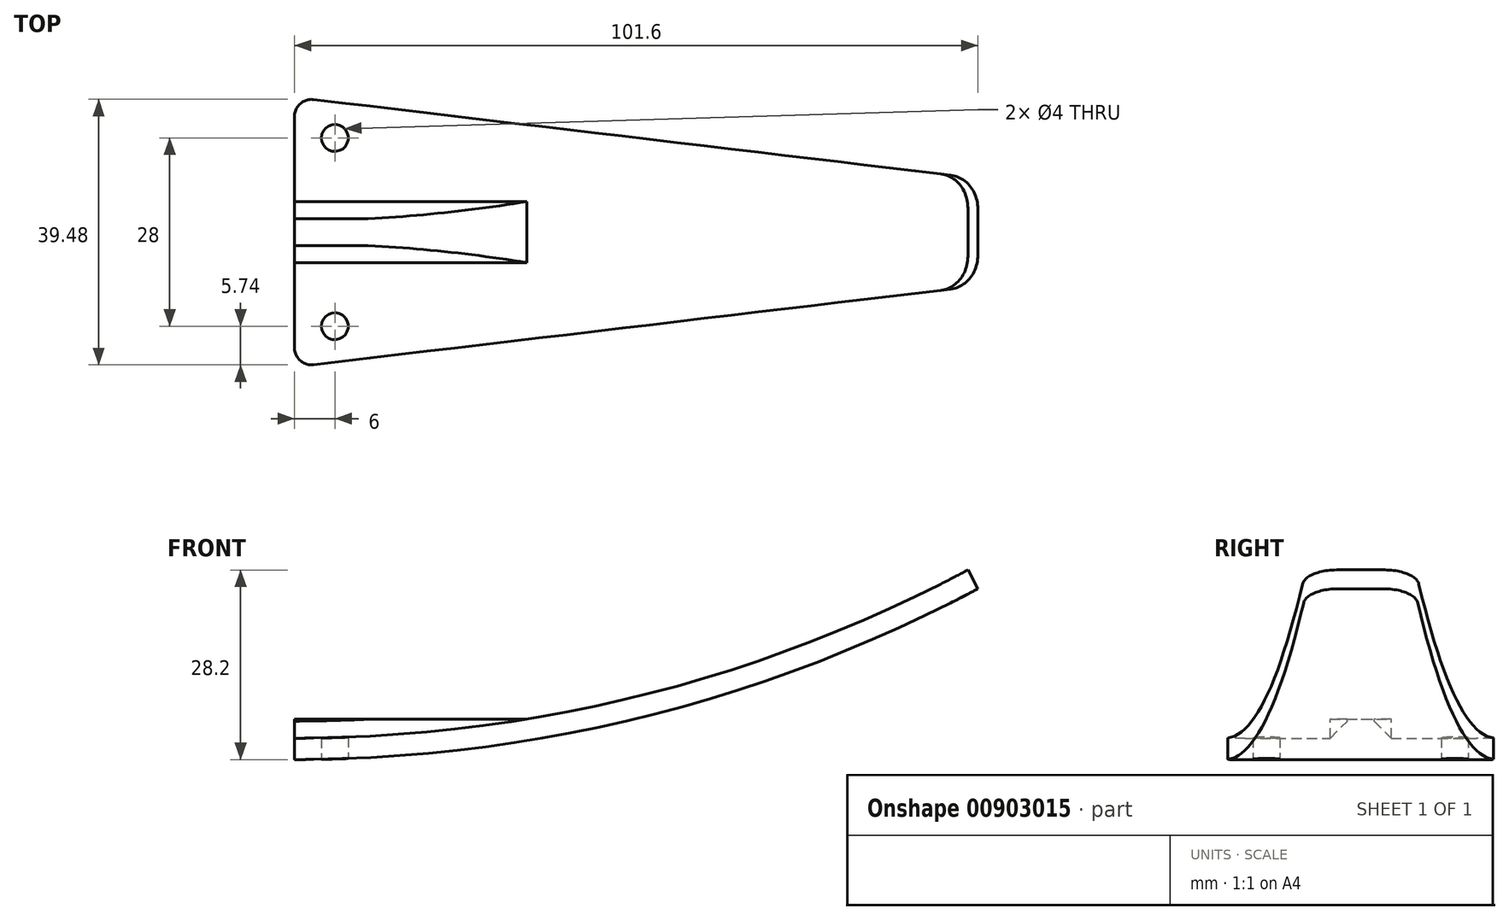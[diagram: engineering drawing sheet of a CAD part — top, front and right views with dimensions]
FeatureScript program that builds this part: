
annotation { "Feature Type Name" : "Feature", "Feature Type Description" : "" }
export const myFeature = defineFeature(function(context is Context, id is Id, definition is map)
    precondition{}
    {
        {
            var Q0;
            Q0=qCreatedBy(makeId("Front.planeOp"),FACE);
            var sketch = newSketch(context, id + "F0", { "sketchPlane" : qUnion([Q0])});
            skArc(sketch, "E0", {"start": v(0, 0) * mm, "mid": v(52.36, 6.45) * mm, "end": v(101.6, 25.4) * mm});
            skLineSegment(sketch, "E1", {"start": v(0, 0) * mm, "end": v(114.5, 0) * mm, "construction": true});
            skArc(sketch, "E2.0", {"start": v(0, 3.18) * mm, "mid": v(51.6, 9.53) * mm, "end": v(100.1, 28.2) * mm});
            skLineSegment(sketch, "E3", {"start": v(0, 3.18) * mm, "end": v(0, 0) * mm});
            skLineSegment(sketch, "E4", {"start": v(100.1, 28.2) * mm, "end": v(101.6, 25.4) * mm});
            skSolve(sketch);
        }
        {
            var Q0;
            Q0 = qSketchRegion(id + "F0", true);
            extrude(context, id + "F1", {"entities" : qUnion([Q0]), "depth" : 20 * mm, "offsetDistance" : 25.4 * mm, "hasSecondDirection" : true, "secondDirectionOppositeDirection" : true, "secondDirectionDepth" : 20 * mm});
        }
        {
            var Q0;
            Q0=qCreatedBy(makeId("Top.planeOp"),FACE);
            var sketch = newSketch(context, id + "F2", { "sketchPlane" : qUnion([Q0])});
            skLineSegment(sketch, "E5", {"start": v(0, 0) * mm, "end": v(113.48, 0) * mm, "construction": true});
            skLineSegment(sketch, "E6", {"start": v(6, 18.01) * mm, "end": v(6, -17.81) * mm, "construction": true});
            skCircle(sketch, "E7", {"center": v(6, 14) * mm, "radius": 2 * mm});
            skCircle(sketch, "E8", {"center": v(6, -14) * mm, "radius": 2 * mm});
            skSolve(sketch);
        }
        {
            var Q0;
            Q0 = qSketchRegion(id + "F2", true);
            extrude(context, id + "F3", {"entities" : qUnion([Q0]), "operationType" : NewBodyOperationType.REMOVE, "depth" : 25.4 * mm, "offsetDistance" : 25.4 * mm});
        }
        {
            var Q0;
            Q0=qCreatedBy(makeId("Top.planeOp"),FACE);
            var sketch = newSketch(context, id + "F4", { "sketchPlane" : qUnion([Q0])});
            skLineSegment(sketch, "E9", {"start": v(0, 0) * mm, "end": v(114.81, 0) * mm, "construction": true});
            skLineSegment(sketch, "E10", {"start": v(0.5, 20) * mm, "end": v(0.5, -20) * mm, "construction": true});
            skLineSegment(sketch, "E11.0", {"start": v(101.6, 8) * mm, "end": v(101.6, 20) * mm});
            skLineSegment(sketch, "E12", {"start": v(0.5, 20) * mm, "end": v(101.6, 8) * mm});
            skLineSegment(sketch, "E13", {"start": v(101.6, 20) * mm, "end": v(0.5, 20) * mm});
            skPoint(sketch, "E14.orphan", {"position": v(101.6, -20) * mm});
            skLineSegment(sketch, "E15.MirrorCS", {"start": v(0.5, -20) * mm, "end": v(101.6, -8) * mm});
            skLineSegment(sketch, "E16.MirrorCS", {"start": v(101.6, -20) * mm, "end": v(0.5, -20) * mm});
            skLineSegment(sketch, "E17.MirrorCS", {"start": v(101.6, -8) * mm, "end": v(101.6, -20) * mm});
            skSolve(sketch);
        }
        {
            var Q0;
            Q0 = qSketchRegion(id + "F4", true);
            extrude(context, id + "F5", {"entities" : qUnion([Q0]), "operationType" : NewBodyOperationType.REMOVE, "depth" : 50.8 * mm, "offsetDistance" : 25.4 * mm});
        }
        {
            var Q0;
            Q0=qCreatedBy(makeId("Front.planeOp"),FACE);
            var sketch = newSketch(context, id + "F6", { "sketchPlane" : qUnion([Q0])});
            skLineSegment(sketch, "E18", {"start": v(0, 0) * mm, "end": v(0, 6) * mm});
            skLineSegment(sketch, "E19", {"start": v(0, 6) * mm, "end": v(37, 6) * mm});
            skLineSegment(sketch, "E20", {"start": v(37, 6) * mm, "end": v(0, 0) * mm});
            skSolve(sketch);
        }
        {
            var Q0;
            Q0 = qSketchRegion(id + "F6", true);
            extrude(context, id + "F7", {"entities" : qUnion([Q0]), "operationType" : NewBodyOperationType.ADD, "depth" : 2 * mm, "offsetDistance" : 25.4 * mm, "hasSecondDirection" : true, "secondDirectionOppositeDirection" : true, "secondDirectionDepth" : 2 * mm});
        }
        {
            var Q0;
            Q0=makeQuery(id+"F7.boolean.opBoolean","INTERSECT",EDGE,{"derivedFrom":[makeQuery(id+"F1.opExtrude","SWEPT_FACE",FACE,{"disambiguationData":[OSD([sQuery(id+"F0.wireOp",EDGE,"E2.0")])]}),makeQuery(id+"F7.opExtrude","CAP_FACE",FACE,{"disambiguationData":[OSD([sQuery(id+"F6.wireOp",EDGE,"E18"),sQuery(id+"F6.wireOp",EDGE,"E19"),sQuery(id+"F6.wireOp",EDGE,"E20")])],"isStart":false})]});
            var Q1;
            Q1=makeQuery(id+"F7.boolean.opBoolean","INTERSECT",EDGE,{"derivedFrom":[makeQuery(id+"F1.opExtrude","SWEPT_FACE",FACE,{"disambiguationData":[OSD([sQuery(id+"F0.wireOp",EDGE,"E2.0")])]}),makeQuery(id+"F7.opExtrude","CAP_FACE",FACE,{"disambiguationData":[OSD([sQuery(id+"F6.wireOp",EDGE,"E18"),sQuery(id+"F6.wireOp",EDGE,"E19"),sQuery(id+"F6.wireOp",EDGE,"E20")])],"isStart":true})]});
            chamfer(context, id + "F8", {"entities" : qUnion([Q0, Q1]), "width" : 2.54 * mm, "tangentPropagation" : true});
        }
        {
            var Q0;
            Q0=makeQuery(id+"F5.boolean.opBoolean","INTERSECT",EDGE,{"derivedFrom":[makeQuery(id+"F1.opExtrude","SWEPT_FACE",FACE,{"disambiguationData":[OSD([sQuery(id+"F0.wireOp",EDGE,"E4")])]}),makeQuery(id+"F5.opExtrude","SWEPT_FACE",FACE,{"disambiguationData":[OSD([sQuery(id+"F4.wireOp",EDGE,"E15.MirrorCS")])]})]});
            var Q1;
            Q1=makeQuery(id+"F5.boolean.opBoolean","INTERSECT",EDGE,{"derivedFrom":[makeQuery(id+"F1.opExtrude","SWEPT_FACE",FACE,{"disambiguationData":[OSD([sQuery(id+"F0.wireOp",EDGE,"E4")])]}),makeQuery(id+"F5.opExtrude","SWEPT_FACE",FACE,{"disambiguationData":[OSD([sQuery(id+"F4.wireOp",EDGE,"E12")])]})]});
            fillet(context, id + "F9", {"entities" : qUnion([Q0, Q1]), "radius" : 5.08 * mm, "tangentPropagation" : true, "allowEdgeOverflow" : false});
        }
        {
            var Q0;
            Q0=makeQuery(id+"F1.opExtrude","CAP_EDGE",EDGE,{"disambiguationData":[OSD([sQuery(id+"F0.wireOp",EDGE,"E3")])],"isStart":false});
            var Q1;
            Q1=makeQuery(id+"F1.opExtrude","CAP_EDGE",EDGE,{"disambiguationData":[OSD([sQuery(id+"F0.wireOp",EDGE,"E3")])],"isStart":true});
            fillet(context, id + "F10", {"entities" : qUnion([Q0, Q1]), "radius" : 2.54 * mm, "tangentPropagation" : true, "allowEdgeOverflow" : false});
        }
        {
            var Q0;
            Q0=makeQuery(id+"F10.opFillet","BLEND_EDGE",EDGE,{"blendedFrom":[makeQuery(id+"F1.opExtrude","CAP_EDGE",EDGE,{"disambiguationData":[OSD([sQuery(id+"F0.wireOp",EDGE,"E3")])],"isStart":false}),makeQuery(id+"F5.boolean.opBoolean","COPY",FACE,{"derivedFrom":makeQuery(id+"F5.opExtrude","SWEPT_FACE",FACE,{"disambiguationData":[OSD([sQuery(id+"F4.wireOp",EDGE,"E15.MirrorCS")])]})})],"blendedInto":[makeQuery(id+"F5.boolean.opBoolean","COPY",FACE,{"derivedFrom":makeQuery(id+"F5.opExtrude","SWEPT_FACE",FACE,{"disambiguationData":[OSD([sQuery(id+"F4.wireOp",EDGE,"E15.MirrorCS")])]})})]});
            var Q1;
            Q1=makeQuery(id+"F10.opFillet","BLEND_EDGE",EDGE,{"blendedFrom":[makeQuery(id+"F1.opExtrude","CAP_EDGE",EDGE,{"disambiguationData":[OSD([sQuery(id+"F0.wireOp",EDGE,"E3")])],"isStart":true}),makeQuery(id+"F5.boolean.opBoolean","COPY",FACE,{"derivedFrom":makeQuery(id+"F5.opExtrude","SWEPT_FACE",FACE,{"disambiguationData":[OSD([sQuery(id+"F4.wireOp",EDGE,"E12")])]})})],"blendedInto":[makeQuery(id+"F5.boolean.opBoolean","COPY",FACE,{"derivedFrom":makeQuery(id+"F5.opExtrude","SWEPT_FACE",FACE,{"disambiguationData":[OSD([sQuery(id+"F4.wireOp",EDGE,"E12")])]})})]});
            fillet(context, id + "F11", {"entities" : qUnion([Q0, Q1]), "radius" : 2.54 * mm, "tangentPropagation" : true, "allowEdgeOverflow" : false});
        }
    });
